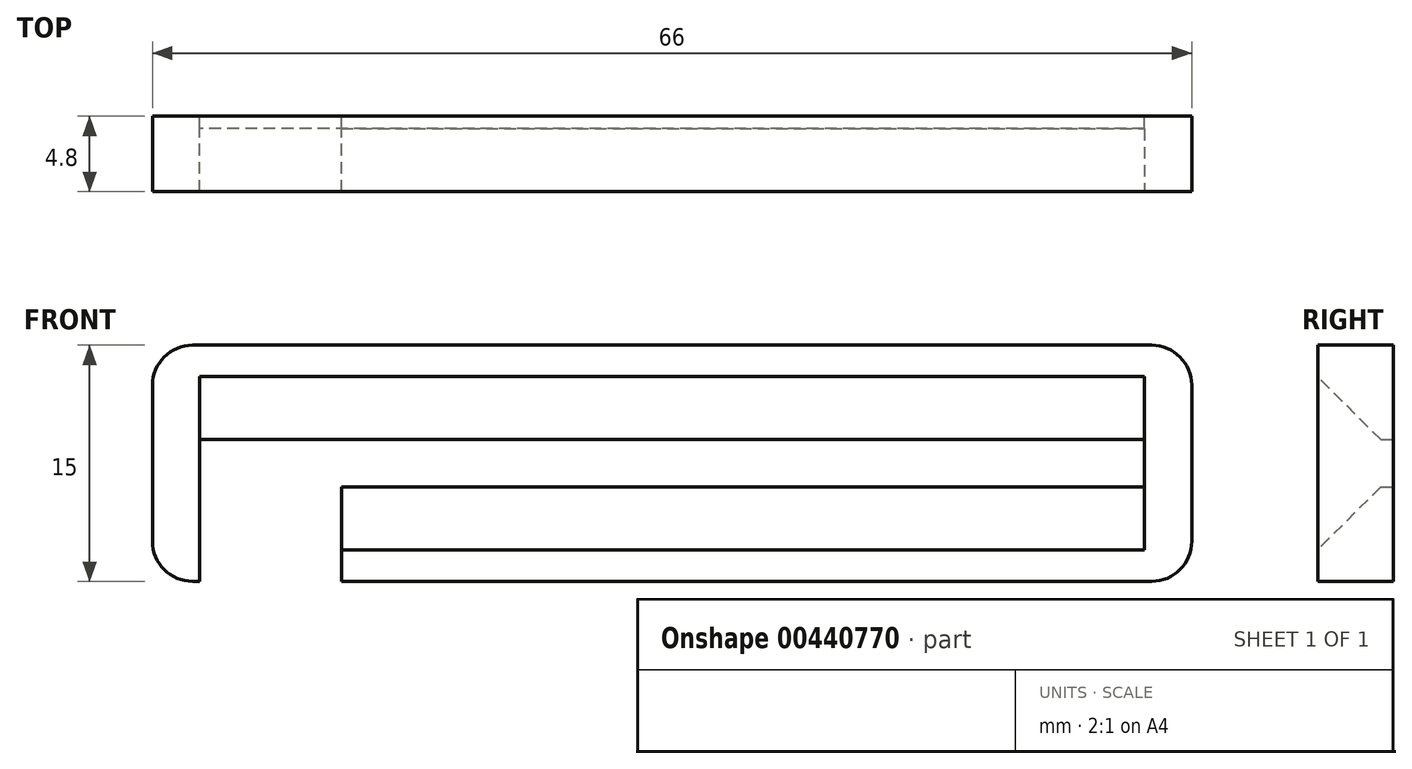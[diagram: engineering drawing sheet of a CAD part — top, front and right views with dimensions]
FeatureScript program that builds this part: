
annotation { "Feature Type Name" : "Feature", "Feature Type Description" : "" }
export const myFeature = defineFeature(function(context is Context, id is Id, definition is map)
    precondition{}
    {
        {
            var Q0;
            Q0=qCreatedBy(makeId("Front.planeOp"),FACE);
            var sketch = newSketch(context, id + "F0", { "sketchPlane" : qUnion([Q0])});
            skLineSegment(sketch, "E0.bottom", {"start": v(30.46, 7.5) * mm, "end": v(-30.46, 7.5) * mm});
            skLineSegment(sketch, "E0.top", {"start": v(30.46, -7.5) * mm, "end": v(-30.46, -7.5) * mm});
            skLineSegment(sketch, "E0.left", {"start": v(33, 4.96) * mm, "end": v(33, -4.96) * mm});
            skLineSegment(sketch, "E0.right", {"start": v(-33, 4.96) * mm, "end": v(-33, -4.96) * mm});
            skPoint(sketch, "E0.middle", {"position": v(0, 0) * mm});
            skLineSegment(sketch, "E1.bottom", {"start": v(27.46, -4.5) * mm, "end": v(-27.46, -4.5) * mm});
            skLineSegment(sketch, "E1.top", {"start": v(27.46, 4.5) * mm, "end": v(-27.46, 4.5) * mm});
            skLineSegment(sketch, "E1.left", {"start": v(30, -1.96) * mm, "end": v(30, 1.96) * mm});
            skLineSegment(sketch, "E1.right", {"start": v(-30, -1.96) * mm, "end": v(-30, 1.96) * mm});
            skPoint(sketch, "E2.visualSharp", {"position": v(-33, 7.5) * mm});
            skArc(sketch, "E2.filletArc", {"start": v(-30.46, 7.5) * mm, "mid": v(-32.26, 6.76) * mm, "end": v(-33, 4.96) * mm});
            skPoint(sketch, "E3.visualSharp", {"position": v(-33, -7.5) * mm});
            skArc(sketch, "E3.filletArc", {"start": v(-33, -4.96) * mm, "mid": v(-32.26, -6.76) * mm, "end": v(-30.46, -7.5) * mm});
            skPoint(sketch, "E4.visualSharp", {"position": v(33, 7.5) * mm});
            skArc(sketch, "E4.filletArc", {"start": v(33, 4.96) * mm, "mid": v(32.26, 6.76) * mm, "end": v(30.46, 7.5) * mm});
            skPoint(sketch, "E5.visualSharp", {"position": v(33, -7.5) * mm});
            skArc(sketch, "E5.filletArc", {"start": v(30.46, -7.5) * mm, "mid": v(32.26, -6.76) * mm, "end": v(33, -4.96) * mm});
            skPoint(sketch, "E6.visualSharp", {"position": v(30, -4.5) * mm});
            skArc(sketch, "E6.filletArc", {"start": v(27.46, -4.5) * mm, "mid": v(29.26, -3.76) * mm, "end": v(30, -1.96) * mm});
            skPoint(sketch, "E7.visualSharp", {"position": v(-30, -4.5) * mm});
            skArc(sketch, "E7.filletArc", {"start": v(-30, -1.96) * mm, "mid": v(-29.26, -3.76) * mm, "end": v(-27.46, -4.5) * mm});
            skPoint(sketch, "E8.visualSharp", {"position": v(30, 4.5) * mm});
            skArc(sketch, "E8.filletArc", {"start": v(30, 1.96) * mm, "mid": v(29.26, 3.76) * mm, "end": v(27.46, 4.5) * mm});
            skPoint(sketch, "E9.visualSharp", {"position": v(-30, 4.5) * mm});
            skArc(sketch, "E9.filletArc", {"start": v(-27.46, 4.5) * mm, "mid": v(-29.26, 3.76) * mm, "end": v(-30, 1.96) * mm});
            skLineSegment(sketch, "E10.bottom", {"start": v(30, -1.5) * mm, "end": v(-30, -1.5) * mm});
            skLineSegment(sketch, "E10.top", {"start": v(30, 1.5) * mm, "end": v(-30, 1.5) * mm});
            skLineSegment(sketch, "E10.left", {"start": v(30, -1.5) * mm, "end": v(30, 1.5) * mm});
            skLineSegment(sketch, "E10.right", {"start": v(-30, -1.5) * mm, "end": v(-30, 1.5) * mm});
            skLineSegment(sketch, "E11.bottom", {"start": v(-30, 1.5) * mm, "end": v(-21, 1.5) * mm});
            skLineSegment(sketch, "E11.top", {"start": v(-30, -7.5) * mm, "end": v(-21, -7.5) * mm});
            skLineSegment(sketch, "E11.left", {"start": v(-30, 1.5) * mm, "end": v(-30, -7.5) * mm});
            skLineSegment(sketch, "E11.right", {"start": v(-21, 1.5) * mm, "end": v(-21, -7.5) * mm});
            skSolve(sketch);
        }
        {
            var Q0;
            Q0=makeQuery(id+"F0.imprint","IMPRINT",FACE,{"disambiguationData":[TD([[makeQuery(id+"F0.imprint","IMPRINT",EDGE,{"derivedFrom":sQuery(id+"F0.wireOp",EDGE,"E0.bottom")}),1.0]])]});
            var Q1;
            {var subQ5=sQuery(id+"F0.wireOp",EDGE,"E6.filletArc");Q1=makeQuery(id+"F0.imprint","IMPRINT",FACE,{"disambiguationData":[TD([[makeQuery(id+"F0.imprint","IMPRINT",EDGE,{"derivedFrom":subQ5}),1.0]])]});}
            var Q2;
            Q2=makeQuery(id+"F0.imprint","IMPRINT",FACE,{"disambiguationData":[TD([[makeQuery(id+"F0.imprint","IMPRINT",EDGE,{"derivedFrom":sQuery(id+"F0.wireOp",EDGE,"E1.top")}),1.0]])]});
            extrude(context, id + "F1", {"entities" : qUnion([Q0, Q1, Q2]), "depth" : 4.8 * mm});
        }
        {
            var Q0;
            Q0=makeQuery(id+"F1.opExtrude","CAP_EDGE",EDGE,{"disambiguationData":[OSD([sQuery(id+"F0.wireOp",EDGE,"E10.top"),sQuery(id+"F0.wireOp",EDGE,"E11.bottom")])],"isStart":false});
            var Q1;
            Q1=makeQuery(id+"F1.opExtrude","CAP_EDGE",EDGE,{"disambiguationData":[OSD([sQuery(id+"F0.wireOp",EDGE,"E10.bottom")])],"isStart":false});
            chamfer(context, id + "F2", {"entities" : qUnion([Q0, Q1]), "chamferType" : ChamferType.OFFSET_ANGLE, "width" : 4 * mm, "oppositeDirection" : false, "angle" : 45 * degree, "tangentPropagation" : true});
        }
    });
